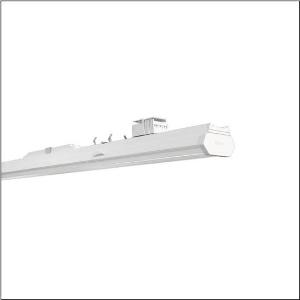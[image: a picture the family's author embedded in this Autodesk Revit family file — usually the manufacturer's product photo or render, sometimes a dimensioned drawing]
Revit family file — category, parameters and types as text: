
# Revit family: licross_r__11_protected_mo_51td11cn49xg_045e
name_source: partatom
category: Lighting Fixtures
units: mm (PartAtom-declared; Revit-internal decimal feet)

## family parameters
Cut with Voids When Loaded = No
Host = Face
Light Source = No
Part Type = Normal
Room Calculation Point = No
Round Connector Dimension = Use Diameter
Shared = No

## types (1)
- --- (1 x LED, 9030 lm, 49.4 W, 4000K)
    Apparent Load = 49 VA
    CIE Flux Codes = 83 94 98 100 100
    Color Rendering = 80
    Color Temperature = 4000K
    Default Elevation = 1800 mm
    Description = Licross® 11 Protected MO, luminaire insert, of sheet steel, galvanised, coil coated, white, length: 1.500mm, width: 90mm, height: 101mm, LED rated luminous flux: 9.030lm, light colour: 840, control gear: ON/OFF Multilumen, CLOi, with plug, 3-pole, with phase selection, mains connection: 220..240V, AC, 50/60Hz, start of lifetime: 49W, end of service life: 55W, halogen-free wiring, primary light control with lens, of plastic, primary optical cover: cover, of PMMA, light emission: direct distribution, primary light characteristic: symmetric, protection rating (complete): IP54, insulation class (complete): insulation class I (protective earthing), certification: CE, ENEC, VDE, UKCA, protection symbol: D if used in an environment with non-conductive dust loads with corresponding accessories, impact resistance: IK06, permissible ambient temperature for indoor applications: -35..+40°C, corresponds to IFS (International Featured Standards) requirements for safety and quality in the food industry, reducing of maximum allowable ambient temperature of 5°C with ceiling mounting, LABS conformity tested according to VDMA 24364:2018-05, packaging unit: 1 piece
    Height = 92 mm
    Lamp = 1 x LED
    Lamp Light Flux = 9030 lm
    Lamp Power = 49.4 W
    Lamp count = 1
    Length = 1500 mm
    Luminous efficacy = 183 lm/W
    Manufacturer = Siteco
    ModVariant = No
    Model = 51TD11CN49XG
    Mounting Place = Ceiling
    Mounting Type = Pendant
    Number of Poles = 1
    OnlyDefault = Yes
    Power Factor = 1
    Product Name = Licross® 11 Protected MO
    Product group = luminaire insert
    ProductGroupID = 901
    Protection Class = Protection class I
    Protection Degree = IP 54
    RLX_Detail_Level = 1
    RLX_Emergency_Light_Flux = 0 lm
    RLX_Emergency_Type = 0
    RLX_Emergency_Type_DB = No
    RlxData = <blob elided: 21893 chars, md5=62eb2f54>
    Socket = socket
    Standby Power = 0 W
    System Light Flux = 9030 lm
    System Power = 49 W
    Type Comments = factory setting: luminous flux: 100 % | (A | C | E) | 113 mA
    Type Image = l_1256145.jpg
    URL = http://relux.com
    VarID = @adj_037957
    Voltage = 0 V
    Weight = 0.00 kg
    Width = 88 mm

## geometry (parser evidence)
native form markers: Blend x4, Sweep x11
no freeform markers — native parametric forms only
